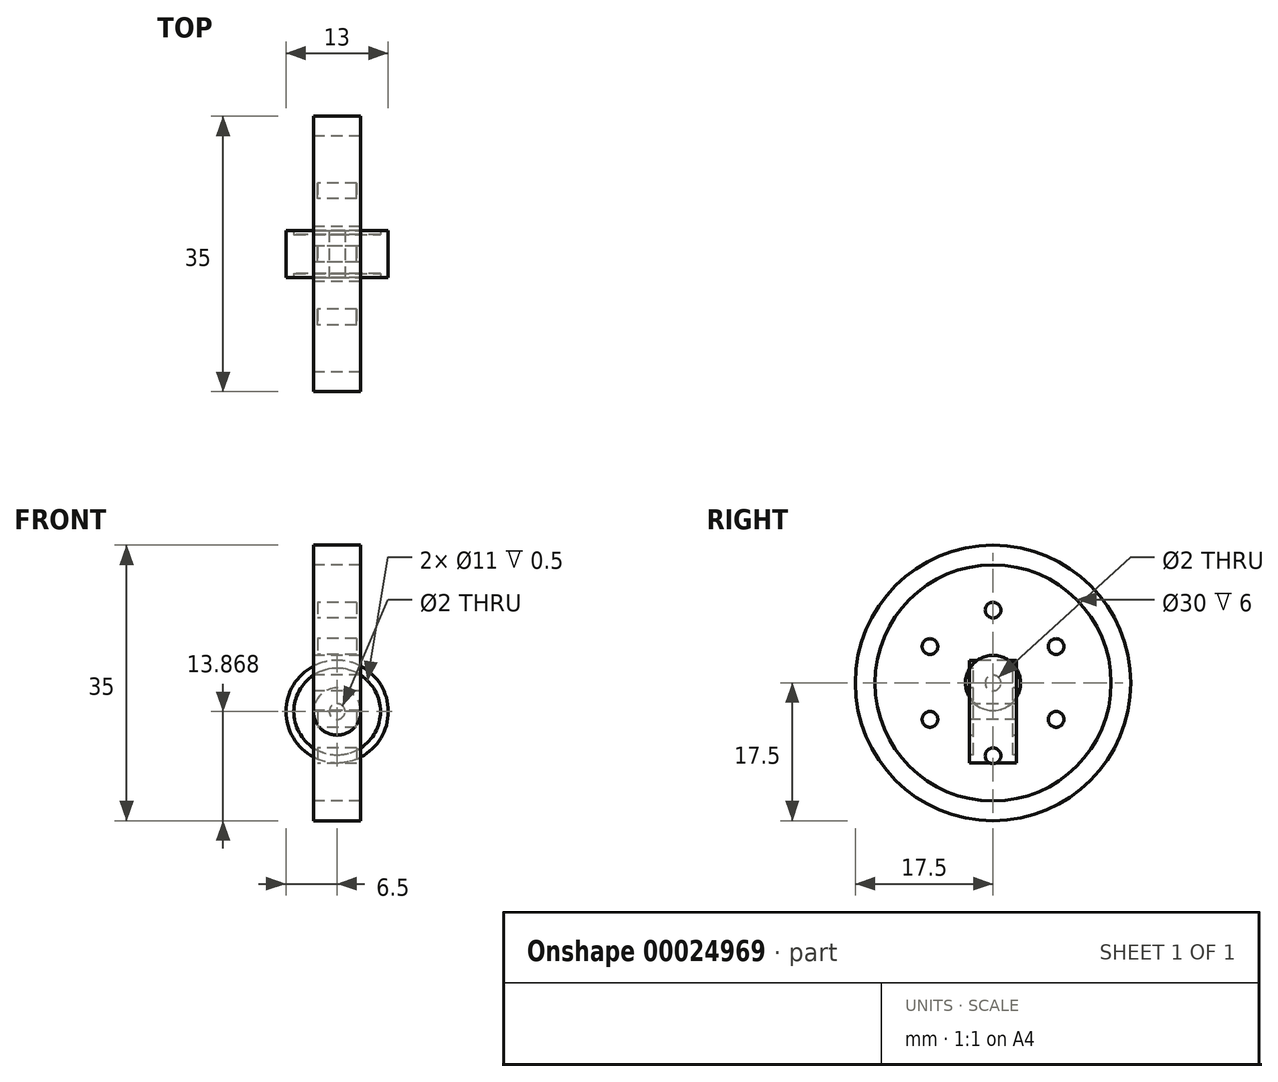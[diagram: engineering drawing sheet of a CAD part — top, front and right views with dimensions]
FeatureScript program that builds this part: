
annotation { "Feature Type Name" : "Feature", "Feature Type Description" : "" }
export const myFeature = defineFeature(function(context is Context, id is Id, definition is map)
    precondition{}
    {
        {
            var Q0;
            Q0=qCreatedBy(makeId("Front.planeOp"),FACE);
            var sketch = newSketch(context, id + "F0", { "sketchPlane" : qUnion([Q0])});
            skLineSegment(sketch, "E0", {"start": v(-52.2, 0) * mm, "end": v(47.8, 0) * mm, "construction": true});
            skLineSegment(sketch, "E1", {"start": v(0, 0) * mm, "end": v(0, 1) * mm, "construction": true});
            skLineSegment(sketch, "E2.rect.bottom", {"start": v(3, 1) * mm, "end": v(-3, 1) * mm});
            skLineSegment(sketch, "E2.rect.top", {"start": v(3, 3.5) * mm, "end": v(-3, 3.5) * mm});
            skLineSegment(sketch, "E2.rect.left", {"start": v(3, 1) * mm, "end": v(3, 3.5) * mm});
            skLineSegment(sketch, "E2.rect.right", {"start": v(-3, 1) * mm, "end": v(-3, 3.5) * mm});
            skPoint(sketch, "E2.rect.middle", {"position": v(0, 2.25) * mm});
            skLineSegment(sketch, "E3.rect.bottom", {"start": v(-2.5, 3.5) * mm, "end": v(2.5, 3.5) * mm});
            skLineSegment(sketch, "E3.rect.top", {"start": v(-2.5, 15) * mm, "end": v(2.5, 15) * mm});
            skLineSegment(sketch, "E3.rect.left", {"start": v(-2.5, 3.5) * mm, "end": v(-2.5, 15) * mm});
            skLineSegment(sketch, "E3.rect.right", {"start": v(2.5, 3.5) * mm, "end": v(2.5, 15) * mm});
            skPoint(sketch, "E3.rect.middle", {"position": v(0, 9.25) * mm});
            skLineSegment(sketch, "E4.rect.bottom", {"start": v(-3, 15) * mm, "end": v(3, 15) * mm});
            skLineSegment(sketch, "E4.rect.top", {"start": v(-3, 17.5) * mm, "end": v(3, 17.5) * mm});
            skLineSegment(sketch, "E4.rect.left", {"start": v(-3, 15) * mm, "end": v(-3, 17.5) * mm});
            skLineSegment(sketch, "E4.rect.right", {"start": v(3, 15) * mm, "end": v(3, 17.5) * mm});
            skPoint(sketch, "E4.rect.middle", {"position": v(0, 16.25) * mm});
            skSolve(sketch);
        }
        {
            var Q0;
            Q0 = qSketchRegion(id + "F0", true);
            var Q1;
            Q1=sQuery(id+"F0.wireOp",EDGE,"E0");
            revolve(context, id + "F1", {"entities" : qUnion([Q0]), "axis" : qUnion([Q1]), "revolveType" : RevolveType.FULL});
        }
        {
            var Q0;
            Q0=makeQuery(id+"F1.opRevolve","SWEPT_FACE",FACE,{"disambiguationData":[OSD([sQuery(id+"F0.wireOp",EDGE,"E3.rect.left")])]});
            var sketch = newSketch(context, id + "F2", { "sketchPlane" : qUnion([Q0])});
            skCircle(sketch, "E5", {"center": v(0, 0) * mm, "radius": 9.25 * mm});
            skArc(sketch, "E6.1.3.0", {"start": v(-7.46, 5.46) * mm, "mid": v(4.63, -8.01) * mm, "end": v(-1, 9.2) * mm});
            skArc(sketch, "E6.1.4.0", {"start": v(-7.46, 5.46) * mm, "mid": v(4.19, -8.25) * mm, "end": v(0, 9.25) * mm});
            skArc(sketch, "E6.1.5.0", {"start": v(-7.46, 5.46) * mm, "mid": v(4.62, -8.01) * mm, "end": v(-1, 9.2) * mm});
            skCircle(sketch, "E7", {"center": v(0, 9.25) * mm, "radius": 1 * mm});
            skCircle(sketch, "E8.1.0", {"center": v(-8.01, 4.63) * mm, "radius": 1 * mm});
            skCircle(sketch, "E8.2.0", {"center": v(-8.01, -4.62) * mm, "radius": 1 * mm});
            skCircle(sketch, "E8.3.0", {"center": v(0, -9.25) * mm, "radius": 1 * mm});
            skCircle(sketch, "E8.4.0", {"center": v(8.01, -4.63) * mm, "radius": 1 * mm});
            skCircle(sketch, "E8.5.0", {"center": v(8.01, 4.63) * mm, "radius": 1 * mm});
            skSolve(sketch);
        }
        {
            var Q0;
            {var subQ0=sQuery(id+"F2.wireOp",EDGE,"E8.1.0");var subQ1=sQuery(id+"F2.wireOp",EDGE,"E5");var subQ3=makeQuery(id+"F2.imprint","INTERSECT",VERTEX,{"disambiguationData":[OD(0.0)],"derivedFrom":[subQ1,subQ0]});Q0=makeQuery(id+"F2.imprint","IMPRINT",FACE,{"disambiguationData":[TD([[makeQuery(id+"F2.imprint","IMPRINT",EDGE,{"disambiguationData":[TD([[subQ3,1.0]])],"derivedFrom":subQ1}),-1.0]])]});}
            var Q1;
            {var subQ0=sQuery(id+"F2.wireOp",EDGE,"E8.1.0");var subQ1=sQuery(id+"F2.wireOp",EDGE,"E5");var subQ3=makeQuery(id+"F2.imprint","INTERSECT",VERTEX,{"disambiguationData":[OD(0.0)],"derivedFrom":[subQ1,subQ0]});Q1=makeQuery(id+"F2.imprint","IMPRINT",FACE,{"disambiguationData":[TD([[makeQuery(id+"F2.imprint","IMPRINT",EDGE,{"disambiguationData":[TD([[subQ3,1.0]])],"derivedFrom":subQ1}),1.0]])]});}
            var Q2;
            {var subQ1=sQuery(id+"F2.wireOp",EDGE,"E5");var subQ4=makeQuery(id+"F2.imprint","IMPRINT",VERTEX,{"derivedFrom":subQ1});Q2=makeQuery(id+"F2.imprint","IMPRINT",FACE,{"disambiguationData":[TD([[makeQuery(id+"F2.imprint","IMPRINT",EDGE,{"disambiguationData":[TD([[subQ4,1.0]])],"derivedFrom":subQ1}),-1.0]])]});}
            var Q3;
            {var subQ1=sQuery(id+"F2.wireOp",EDGE,"E5");var subQ4=makeQuery(id+"F2.imprint","IMPRINT",VERTEX,{"derivedFrom":subQ1});Q3=makeQuery(id+"F2.imprint","IMPRINT",FACE,{"disambiguationData":[TD([[makeQuery(id+"F2.imprint","IMPRINT",EDGE,{"disambiguationData":[TD([[subQ4,1.0]])],"derivedFrom":subQ1}),1.0]])]});}
            var Q4;
            {var subQ0=sQuery(id+"F2.wireOp",EDGE,"E8.5.0");var subQ1=sQuery(id+"F2.wireOp",EDGE,"E5");var subQ3=makeQuery(id+"F2.imprint","INTERSECT",VERTEX,{"disambiguationData":[OD(0.0)],"derivedFrom":[subQ1,subQ0]});Q4=makeQuery(id+"F2.imprint","IMPRINT",FACE,{"disambiguationData":[TD([[makeQuery(id+"F2.imprint","IMPRINT",EDGE,{"disambiguationData":[TD([[subQ3,-1.0]])],"derivedFrom":subQ1}),-1.0]])]});}
            var Q5;
            {var subQ0=sQuery(id+"F2.wireOp",EDGE,"E8.5.0");var subQ1=sQuery(id+"F2.wireOp",EDGE,"E5");var subQ3=makeQuery(id+"F2.imprint","INTERSECT",VERTEX,{"disambiguationData":[OD(0.0)],"derivedFrom":[subQ1,subQ0]});Q5=makeQuery(id+"F2.imprint","IMPRINT",FACE,{"disambiguationData":[TD([[makeQuery(id+"F2.imprint","IMPRINT",EDGE,{"disambiguationData":[TD([[subQ3,-1.0]])],"derivedFrom":subQ1}),1.0]])]});}
            var Q6;
            {var subQ0=sQuery(id+"F2.wireOp",EDGE,"E8.4.0");var subQ1=sQuery(id+"F2.wireOp",EDGE,"E5");var subQ3=makeQuery(id+"F2.imprint","INTERSECT",VERTEX,{"disambiguationData":[OD(0.0)],"derivedFrom":[subQ1,subQ0]});Q6=makeQuery(id+"F2.imprint","IMPRINT",FACE,{"disambiguationData":[TD([[makeQuery(id+"F2.imprint","IMPRINT",EDGE,{"disambiguationData":[TD([[subQ3,-1.0]])],"derivedFrom":subQ1}),-1.0]])]});}
            var Q7;
            {var subQ0=sQuery(id+"F2.wireOp",EDGE,"E8.4.0");var subQ1=sQuery(id+"F2.wireOp",EDGE,"E5");var subQ3=makeQuery(id+"F2.imprint","INTERSECT",VERTEX,{"disambiguationData":[OD(0.0)],"derivedFrom":[subQ1,subQ0]});Q7=makeQuery(id+"F2.imprint","IMPRINT",FACE,{"disambiguationData":[TD([[makeQuery(id+"F2.imprint","IMPRINT",EDGE,{"disambiguationData":[TD([[subQ3,-1.0]])],"derivedFrom":subQ1}),1.0]])]});}
            var Q8;
            {var subQ0=sQuery(id+"F2.wireOp",EDGE,"E8.2.0");var subQ1=sQuery(id+"F2.wireOp",EDGE,"E5");var subQ3=makeQuery(id+"F2.imprint","INTERSECT",VERTEX,{"disambiguationData":[OD(0.0)],"derivedFrom":[subQ1,subQ0]});Q8=makeQuery(id+"F2.imprint","IMPRINT",FACE,{"disambiguationData":[TD([[makeQuery(id+"F2.imprint","IMPRINT",EDGE,{"disambiguationData":[TD([[subQ3,-1.0]])],"derivedFrom":subQ1}),-1.0]])]});}
            var Q9;
            {var subQ0=sQuery(id+"F2.wireOp",EDGE,"E8.2.0");var subQ1=sQuery(id+"F2.wireOp",EDGE,"E5");var subQ3=makeQuery(id+"F2.imprint","INTERSECT",VERTEX,{"disambiguationData":[OD(0.0)],"derivedFrom":[subQ1,subQ0]});Q9=makeQuery(id+"F2.imprint","IMPRINT",FACE,{"disambiguationData":[TD([[makeQuery(id+"F2.imprint","IMPRINT",EDGE,{"disambiguationData":[TD([[subQ3,-1.0]])],"derivedFrom":subQ1}),1.0]])]});}
            var Q10;
            {var subQ0=sQuery(id+"F2.wireOp",EDGE,"E8.3.0");var subQ1=sQuery(id+"F2.wireOp",EDGE,"E5");var subQ3=makeQuery(id+"F2.imprint","INTERSECT",VERTEX,{"disambiguationData":[OD(0.0)],"derivedFrom":[subQ1,subQ0]});Q10=makeQuery(id+"F2.imprint","IMPRINT",FACE,{"disambiguationData":[TD([[makeQuery(id+"F2.imprint","IMPRINT",EDGE,{"disambiguationData":[TD([[subQ3,-1.0]])],"derivedFrom":subQ1}),1.0]])]});}
            var Q11;
            {var subQ0=sQuery(id+"F2.wireOp",EDGE,"E8.3.0");var subQ1=sQuery(id+"F2.wireOp",EDGE,"E5");var subQ3=makeQuery(id+"F2.imprint","INTERSECT",VERTEX,{"disambiguationData":[OD(0.0)],"derivedFrom":[subQ1,subQ0]});Q11=makeQuery(id+"F2.imprint","IMPRINT",FACE,{"disambiguationData":[TD([[makeQuery(id+"F2.imprint","IMPRINT",EDGE,{"disambiguationData":[TD([[subQ3,-1.0]])],"derivedFrom":subQ1}),-1.0]])]});}
            extrude(context, id + "F3", {"entities" : qUnion([Q0, Q1, Q2, Q3, Q4, Q5, Q6, Q7, Q8, Q9, Q10, Q11]), "operationType" : NewBodyOperationType.REMOVE, "endBound" : BoundingType.THROUGH_ALL, "oppositeDirection" : true, "depth" : 25.4 * mm});
        }
        {
            var Q0;
            Q0=qCreatedBy(makeId("Right.planeOp"),FACE);
            var sketch = newSketch(context, id + "F4", { "sketchPlane" : qUnion([Q0])});
            skLineSegment(sketch, "E9", {"start": v(-14.02, -3.63) * mm, "end": v(14.23, -3.63) * mm, "construction": true});
            skLineSegment(sketch, "E10", {"start": v(0, -3.63) * mm, "end": v(0, -2.63) * mm, "construction": true});
            skLineSegment(sketch, "E11.rect.bottom", {"start": v(-3, -2.63) * mm, "end": v(3, -2.63) * mm});
            skLineSegment(sketch, "E11.rect.top", {"start": v(-3, -0.63) * mm, "end": v(3, -0.63) * mm});
            skLineSegment(sketch, "E11.rect.left", {"start": v(-3, -2.63) * mm, "end": v(-3, -0.63) * mm});
            skLineSegment(sketch, "E11.rect.right", {"start": v(3, -2.63) * mm, "end": v(3, -0.63) * mm});
            skPoint(sketch, "E11.rect.middle", {"position": v(0, -1.63) * mm});
            skLineSegment(sketch, "E12.rect.bottom", {"start": v(-2.5, -0.63) * mm, "end": v(2.5, -0.63) * mm});
            skLineSegment(sketch, "E12.rect.top", {"start": v(-2.5, 1.87) * mm, "end": v(2.5, 1.87) * mm});
            skLineSegment(sketch, "E12.rect.left", {"start": v(-2.5, -0.63) * mm, "end": v(-2.5, 1.87) * mm});
            skLineSegment(sketch, "E12.rect.right", {"start": v(2.5, -0.63) * mm, "end": v(2.5, 1.87) * mm});
            skPoint(sketch, "E12.rect.middle", {"position": v(0, 0.62) * mm});
            skLineSegment(sketch, "E13.rect.bottom", {"start": v(-3, 1.87) * mm, "end": v(3, 1.87) * mm});
            skLineSegment(sketch, "E13.rect.top", {"start": v(-3, 2.87) * mm, "end": v(3, 2.87) * mm});
            skLineSegment(sketch, "E13.rect.left", {"start": v(-3, 1.87) * mm, "end": v(-3, 2.87) * mm});
            skLineSegment(sketch, "E13.rect.right", {"start": v(3, 1.87) * mm, "end": v(3, 2.87) * mm});
            skPoint(sketch, "E13.rect.middle", {"position": v(0, 2.37) * mm});
            skSolve(sketch);
        }
        {
            var Q0;
            Q0 = qSketchRegion(id + "F4", true);
            var Q1;
            Q1=sQuery(id+"F4.wireOp",EDGE,"E9");
            revolve(context, id + "F5", {"entities" : qUnion([Q0]), "axis" : qUnion([Q1]), "revolveType" : RevolveType.FULL});
        }
    });
